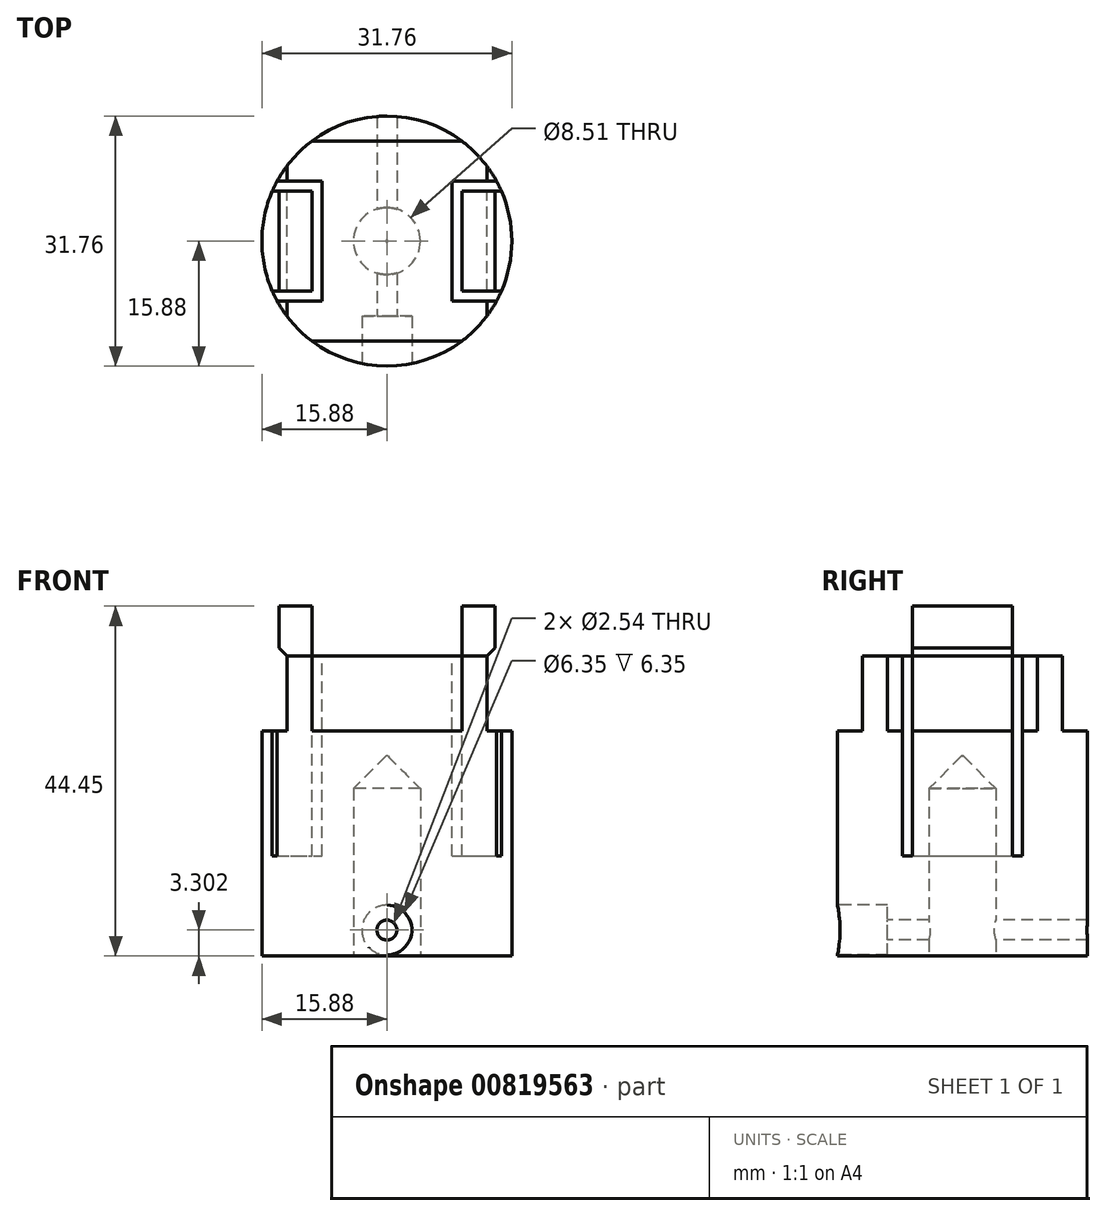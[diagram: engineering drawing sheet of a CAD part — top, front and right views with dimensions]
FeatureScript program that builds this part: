
annotation { "Feature Type Name" : "Feature", "Feature Type Description" : "" }
export const myFeature = defineFeature(function(context is Context, id is Id, definition is map)
    precondition{}
    {
        {
            var Q0;
            Q0=qCreatedBy(makeId("Top.planeOp"),FACE);
            var sketch = newSketch(context, id + "F0", { "sketchPlane" : qUnion([Q0])});
            skCircle(sketch, "E0", {"center": v(0, 0) * mm, "radius": 4.25 * mm});
            skLineSegment(sketch, "E1.bottom", {"start": v(15.88, 15.88) * mm, "end": v(-15.87, 15.88) * mm});
            skLineSegment(sketch, "E1.top", {"start": v(15.87, -15.88) * mm, "end": v(-15.88, -15.88) * mm});
            skLineSegment(sketch, "E1.left", {"start": v(15.88, 15.88) * mm, "end": v(15.88, -15.88) * mm});
            skLineSegment(sketch, "E1.right", {"start": v(-15.88, 15.88) * mm, "end": v(-15.88, -15.88) * mm});
            skSolve(sketch);
        }
        {
            var Q0;
            Q0=makeQuery(id+"F0.imprint","IMPRINT",FACE,{"disambiguationData":[TD([[makeQuery(id+"F0.imprint","IMPRINT",EDGE,{"derivedFrom":sQuery(id+"F0.wireOp",EDGE,"E0")}),-1.0]])]});
            extrude(context, id + "F1", {"entities" : qUnion([Q0]), "depth" : 38.1 * mm, "offsetDistance" : 25.4 * mm});
        }
        {
            var Q0;
            Q0=makeQuery(id+"F1.opExtrude","SWEPT_FACE",FACE,{"disambiguationData":[OSD([sQuery(id+"F0.wireOp",EDGE,"E1.top")])]});
            var sketch = newSketch(context, id + "F2", { "sketchPlane" : qUnion([Q0])});
            skCircle(sketch, "E2", {"center": v(0, 3.3) * mm, "radius": 1.27 * mm});
            skCircle(sketch, "E3", {"center": v(0, 3.3) * mm, "radius": 3.18 * mm});
            skSolve(sketch);
        }
        {
            var Q0;
            Q0=makeQuery(id+"F2.imprint","IMPRINT",FACE,{"disambiguationData":[TD([[makeQuery(id+"F2.imprint","IMPRINT",EDGE,{"derivedFrom":sQuery(id+"F2.wireOp",EDGE,"E2")}),1.0]])]});
            extrude(context, id + "F3", {"entities" : qUnion([Q0]), "operationType" : NewBodyOperationType.REMOVE, "oppositeDirection" : true, "depth" : 76.2 * mm, "offsetDistance" : 25.4 * mm});
        }
        {
            var Q0;
            Q0=makeQuery(id+"F2.imprint","IMPRINT",FACE,{"disambiguationData":[TD([[makeQuery(id+"F2.imprint","IMPRINT",EDGE,{"derivedFrom":sQuery(id+"F2.wireOp",EDGE,"E2")}),-1.0]])]});
            extrude(context, id + "F4", {"entities" : qUnion([Q0]), "operationType" : NewBodyOperationType.REMOVE, "oppositeDirection" : true, "depth" : 6.35 * mm, "offsetDistance" : 25.4 * mm});
        }
        {
            var Q0;
            Q0=makeQuery(id+"F1.opExtrude","CAP_FACE",FACE,{"disambiguationData":[OSD([sQuery(id+"F0.wireOp",EDGE,"E0"),sQuery(id+"F0.wireOp",EDGE,"E1.bottom"),sQuery(id+"F0.wireOp",EDGE,"E1.top"),sQuery(id+"F0.wireOp",EDGE,"E1.left"),sQuery(id+"F0.wireOp",EDGE,"E1.right")])],"isStart":true});
            var sketch = newSketch(context, id + "F5", { "sketchPlane" : qUnion([Q0])});
            skCircle(sketch, "E4", {"center": v(0, 0) * mm, "radius": 15.88 * mm});
            skLineSegment(sketch, "E5.bottom", {"start": v(-15.88, 15.88) * mm, "end": v(15.88, 15.88) * mm});
            skLineSegment(sketch, "E5.top", {"start": v(-15.88, -15.88) * mm, "end": v(15.88, -15.88) * mm});
            skLineSegment(sketch, "E5.left", {"start": v(-15.88, 15.88) * mm, "end": v(-15.88, -15.88) * mm});
            skLineSegment(sketch, "E5.right", {"start": v(15.88, 15.88) * mm, "end": v(15.88, -15.88) * mm});
            skSolve(sketch);
        }
        {
            var Q0;
            Q0=makeQuery(id+"F1.opExtrude","CAP_FACE",FACE,{"disambiguationData":[OSD([sQuery(id+"F0.wireOp",EDGE,"E0"),sQuery(id+"F0.wireOp",EDGE,"E1.bottom"),sQuery(id+"F0.wireOp",EDGE,"E1.top"),sQuery(id+"F0.wireOp",EDGE,"E1.left"),sQuery(id+"F0.wireOp",EDGE,"E1.right")])],"isStart":false});
            var sketch = newSketch(context, id + "F6", { "sketchPlane" : qUnion([Q0])});
            skLineSegment(sketch, "E6.bottom", {"start": v(12.7, -12.7) * mm, "end": v(-12.7, -12.7) * mm});
            skLineSegment(sketch, "E6.top", {"start": v(12.7, 12.7) * mm, "end": v(-12.7, 12.7) * mm});
            skLineSegment(sketch, "E6.left", {"start": v(12.7, -12.7) * mm, "end": v(12.7, 12.7) * mm});
            skLineSegment(sketch, "E6.right", {"start": v(-12.7, -12.7) * mm, "end": v(-12.7, 12.7) * mm});
            skPoint(sketch, "E6.middle", {"position": v(0, 0) * mm});
            skLineSegment(sketch, "E7.bottom", {"start": v(15.88, -15.88) * mm, "end": v(-15.88, -15.88) * mm});
            skLineSegment(sketch, "E7.top", {"start": v(15.88, 15.88) * mm, "end": v(-15.88, 15.87) * mm});
            skLineSegment(sketch, "E7.left", {"start": v(15.88, -15.88) * mm, "end": v(15.88, 15.88) * mm});
            skLineSegment(sketch, "E7.right", {"start": v(-15.88, -15.88) * mm, "end": v(-15.88, 15.88) * mm});
            skSolve(sketch);
        }
        {
            var Q0;
            Q0=makeQuery(id+"F6.imprint","IMPRINT",FACE,{"disambiguationData":[TD([[makeQuery(id+"F6.imprint","IMPRINT",EDGE,{"derivedFrom":sQuery(id+"F6.wireOp",EDGE,"E6.bottom")}),1.0]])]});
            extrude(context, id + "F7", {"entities" : qUnion([Q0]), "operationType" : NewBodyOperationType.REMOVE, "oppositeDirection" : true, "depth" : 9.52 * mm, "offsetDistance" : 25.4 * mm});
        }
        {
            var Q0;
            {var subQ0=sQuery(id+"F5.wireOp",EDGE,"E5.right");var subQ1=sQuery(id+"F5.wireOp",EDGE,"E4");var subQ2=makeQuery(id+"F5.imprint","INTERSECT",VERTEX,{"derivedFrom":[subQ1,subQ0]});Q0=makeQuery(id+"F5.imprint","IMPRINT",FACE,{"disambiguationData":[TD([[makeQuery(id+"F5.imprint","IMPRINT",EDGE,{"disambiguationData":[TD([[subQ2,1.0]])],"derivedFrom":subQ1}),-1.0]])]});}
            var Q1;
            {var subQ0=sQuery(id+"F5.wireOp",EDGE,"E5.left");var subQ1=sQuery(id+"F5.wireOp",EDGE,"E4");var subQ2=makeQuery(id+"F5.imprint","INTERSECT",VERTEX,{"derivedFrom":[subQ1,subQ0]});Q1=makeQuery(id+"F5.imprint","IMPRINT",FACE,{"disambiguationData":[TD([[makeQuery(id+"F5.imprint","IMPRINT",EDGE,{"disambiguationData":[TD([[subQ2,-1.0]])],"derivedFrom":subQ1}),-1.0]])]});}
            var Q2;
            {var subQ0=sQuery(id+"F5.wireOp",EDGE,"E5.bottom");var subQ1=sQuery(id+"F5.wireOp",EDGE,"E4");var subQ2=makeQuery(id+"F5.imprint","INTERSECT",VERTEX,{"derivedFrom":[subQ1,subQ0]});Q2=makeQuery(id+"F5.imprint","IMPRINT",FACE,{"disambiguationData":[TD([[makeQuery(id+"F5.imprint","IMPRINT",EDGE,{"disambiguationData":[TD([[subQ2,-1.0]])],"derivedFrom":subQ1}),-1.0]])]});}
            var Q3;
            {var subQ0=sQuery(id+"F5.wireOp",EDGE,"E5.bottom");var subQ1=sQuery(id+"F5.wireOp",EDGE,"E4");var subQ2=makeQuery(id+"F5.imprint","INTERSECT",VERTEX,{"derivedFrom":[subQ1,subQ0]});Q3=makeQuery(id+"F5.imprint","IMPRINT",FACE,{"disambiguationData":[TD([[makeQuery(id+"F5.imprint","IMPRINT",EDGE,{"disambiguationData":[TD([[subQ2,1.0]])],"derivedFrom":subQ1}),-1.0]])]});}
            extrude(context, id + "F8", {"entities" : qUnion([Q0, Q1, Q2, Q3]), "operationType" : NewBodyOperationType.REMOVE, "oppositeDirection" : true, "depth" : 101.6 * mm, "offsetDistance" : 25.4 * mm});
        }
        {
            var Q0;
            Q0=makeQuery(id+"F1.opExtrude","CAP_FACE",FACE,{"disambiguationData":[OSD([sQuery(id+"F0.wireOp",EDGE,"E0"),sQuery(id+"F0.wireOp",EDGE,"E1.bottom"),sQuery(id+"F0.wireOp",EDGE,"E1.top"),sQuery(id+"F0.wireOp",EDGE,"E1.left"),sQuery(id+"F0.wireOp",EDGE,"E1.right")])],"isStart":false});
            var sketch = newSketch(context, id + "F9", { "sketchPlane" : qUnion([Q0])});
            skLineSegment(sketch, "E8.bottom", {"start": v(-15.88, -7.62) * mm, "end": v(15.88, -7.62) * mm});
            skLineSegment(sketch, "E8.top", {"start": v(-15.88, 7.62) * mm, "end": v(15.88, 7.62) * mm});
            skLineSegment(sketch, "E8.left", {"start": v(-15.88, -7.62) * mm, "end": v(-15.88, 7.62) * mm});
            skLineSegment(sketch, "E8.right", {"start": v(15.88, -7.62) * mm, "end": v(15.88, 7.62) * mm});
            skPoint(sketch, "E8.middle", {"position": v(0, 0) * mm});
            skLineSegment(sketch, "E9.0", {"start": v(8.26, -7.62) * mm, "end": v(8.25, 7.62) * mm});
            skLineSegment(sketch, "E10.0", {"start": v(-8.25, -7.62) * mm, "end": v(-8.26, 7.62) * mm});
            skLineSegment(sketch, "E11.0", {"start": v(-15.88, 6.35) * mm, "end": v(15.88, 6.35) * mm});
            skLineSegment(sketch, "E12.0", {"start": v(-15.88, -6.35) * mm, "end": v(15.88, -6.35) * mm});
            skLineSegment(sketch, "E13.0", {"start": v(-9.52, -7.62) * mm, "end": v(-9.53, 7.62) * mm});
            skLineSegment(sketch, "E14.0", {"start": v(9.53, -7.62) * mm, "end": v(9.52, 7.62) * mm});
            skSolve(sketch);
        }
        {
            var Q0;
            {var subQ0=sQuery(id+"F9.wireOp",EDGE,"E8.left");var subQ1=sQuery(id+"F9.wireOp",EDGE,"E8.top");var subQ2=makeQuery(id+"F9.imprint","INTERSECT",VERTEX,{"derivedFrom":[subQ1,subQ0]});Q0=makeQuery(id+"F9.imprint","IMPRINT",FACE,{"disambiguationData":[TD([[makeQuery(id+"F9.imprint","IMPRINT",EDGE,{"disambiguationData":[TD([[subQ2,-1.0]])],"derivedFrom":subQ1}),-1.0]])]});}
            var Q1;
            {var subQ0=sQuery(id+"F9.wireOp",EDGE,"E13.0");var subQ1=sQuery(id+"F9.wireOp",EDGE,"E8.top");var subQ2=makeQuery(id+"F9.imprint","INTERSECT",VERTEX,{"derivedFrom":[subQ1,subQ0]});Q1=makeQuery(id+"F9.imprint","IMPRINT",FACE,{"disambiguationData":[TD([[makeQuery(id+"F9.imprint","IMPRINT",EDGE,{"disambiguationData":[TD([[subQ2,1.0]])],"derivedFrom":subQ1}),-1.0]])]});}
            var Q2;
            {var subQ0=sQuery(id+"F9.wireOp",EDGE,"E10.0");var subQ1=sQuery(id+"F9.wireOp",EDGE,"E8.top");var subQ2=makeQuery(id+"F9.imprint","INTERSECT",VERTEX,{"derivedFrom":[subQ1,subQ0]});Q2=makeQuery(id+"F9.imprint","IMPRINT",FACE,{"disambiguationData":[TD([[makeQuery(id+"F9.imprint","IMPRINT",EDGE,{"disambiguationData":[TD([[subQ2,1.0]])],"derivedFrom":subQ1}),-1.0]])]});}
            var Q3;
            {var subQ0=sQuery(id+"F9.wireOp",EDGE,"E12.0");var subQ1=sQuery(id+"F9.wireOp",EDGE,"E10.0");var subQ2=makeQuery(id+"F9.imprint","INTERSECT",VERTEX,{"derivedFrom":[subQ1,subQ0]});Q3=makeQuery(id+"F9.imprint","IMPRINT",FACE,{"disambiguationData":[TD([[makeQuery(id+"F9.imprint","IMPRINT",EDGE,{"disambiguationData":[TD([[subQ2,-1.0]])],"derivedFrom":subQ1}),1.0]])]});}
            var Q4;
            {var subQ0=sQuery(id+"F9.wireOp",EDGE,"E10.0");var subQ1=sQuery(id+"F9.wireOp",EDGE,"E8.bottom");var subQ2=makeQuery(id+"F9.imprint","INTERSECT",VERTEX,{"derivedFrom":[subQ1,subQ0]});Q4=makeQuery(id+"F9.imprint","IMPRINT",FACE,{"disambiguationData":[TD([[makeQuery(id+"F9.imprint","IMPRINT",EDGE,{"disambiguationData":[TD([[subQ2,1.0]])],"derivedFrom":subQ1}),1.0]])]});}
            var Q5;
            {var subQ0=sQuery(id+"F9.wireOp",EDGE,"E13.0");var subQ1=sQuery(id+"F9.wireOp",EDGE,"E8.bottom");var subQ2=makeQuery(id+"F9.imprint","INTERSECT",VERTEX,{"derivedFrom":[subQ1,subQ0]});Q5=makeQuery(id+"F9.imprint","IMPRINT",FACE,{"disambiguationData":[TD([[makeQuery(id+"F9.imprint","IMPRINT",EDGE,{"disambiguationData":[TD([[subQ2,1.0]])],"derivedFrom":subQ1}),1.0]])]});}
            var Q6;
            {var subQ0=sQuery(id+"F9.wireOp",EDGE,"E8.left");var subQ1=sQuery(id+"F9.wireOp",EDGE,"E8.bottom");var subQ2=makeQuery(id+"F9.imprint","INTERSECT",VERTEX,{"derivedFrom":[subQ1,subQ0]});Q6=makeQuery(id+"F9.imprint","IMPRINT",FACE,{"disambiguationData":[TD([[makeQuery(id+"F9.imprint","IMPRINT",EDGE,{"disambiguationData":[TD([[subQ2,-1.0]])],"derivedFrom":subQ1}),1.0]])]});}
            var Q7;
            {var subQ0=sQuery(id+"F9.wireOp",EDGE,"E8.right");var subQ1=sQuery(id+"F9.wireOp",EDGE,"E8.top");var subQ2=makeQuery(id+"F9.imprint","INTERSECT",VERTEX,{"derivedFrom":[subQ1,subQ0]});Q7=makeQuery(id+"F9.imprint","IMPRINT",FACE,{"disambiguationData":[TD([[makeQuery(id+"F9.imprint","IMPRINT",EDGE,{"disambiguationData":[TD([[subQ2,1.0]])],"derivedFrom":subQ1}),-1.0]])]});}
            var Q8;
            {var subQ0=sQuery(id+"F9.wireOp",EDGE,"E14.0");var subQ1=sQuery(id+"F9.wireOp",EDGE,"E8.top");var subQ2=makeQuery(id+"F9.imprint","INTERSECT",VERTEX,{"derivedFrom":[subQ1,subQ0]});Q8=makeQuery(id+"F9.imprint","IMPRINT",FACE,{"disambiguationData":[TD([[makeQuery(id+"F9.imprint","IMPRINT",EDGE,{"disambiguationData":[TD([[subQ2,-1.0]])],"derivedFrom":subQ1}),-1.0]])]});}
            var Q9;
            {var subQ0=sQuery(id+"F9.wireOp",EDGE,"E9.0");var subQ1=sQuery(id+"F9.wireOp",EDGE,"E8.top");var subQ2=makeQuery(id+"F9.imprint","INTERSECT",VERTEX,{"derivedFrom":[subQ1,subQ0]});Q9=makeQuery(id+"F9.imprint","IMPRINT",FACE,{"disambiguationData":[TD([[makeQuery(id+"F9.imprint","IMPRINT",EDGE,{"disambiguationData":[TD([[subQ2,-1.0]])],"derivedFrom":subQ1}),-1.0]])]});}
            var Q10;
            {var subQ0=sQuery(id+"F9.wireOp",EDGE,"E12.0");var subQ1=sQuery(id+"F9.wireOp",EDGE,"E9.0");var subQ2=makeQuery(id+"F9.imprint","INTERSECT",VERTEX,{"derivedFrom":[subQ1,subQ0]});Q10=makeQuery(id+"F9.imprint","IMPRINT",FACE,{"disambiguationData":[TD([[makeQuery(id+"F9.imprint","IMPRINT",EDGE,{"disambiguationData":[TD([[subQ2,-1.0]])],"derivedFrom":subQ1}),-1.0]])]});}
            var Q11;
            {var subQ0=sQuery(id+"F9.wireOp",EDGE,"E9.0");var subQ1=sQuery(id+"F9.wireOp",EDGE,"E8.bottom");var subQ2=makeQuery(id+"F9.imprint","INTERSECT",VERTEX,{"derivedFrom":[subQ1,subQ0]});Q11=makeQuery(id+"F9.imprint","IMPRINT",FACE,{"disambiguationData":[TD([[makeQuery(id+"F9.imprint","IMPRINT",EDGE,{"disambiguationData":[TD([[subQ2,-1.0]])],"derivedFrom":subQ1}),1.0]])]});}
            var Q12;
            {var subQ0=sQuery(id+"F9.wireOp",EDGE,"E14.0");var subQ1=sQuery(id+"F9.wireOp",EDGE,"E8.bottom");var subQ2=makeQuery(id+"F9.imprint","INTERSECT",VERTEX,{"derivedFrom":[subQ1,subQ0]});Q12=makeQuery(id+"F9.imprint","IMPRINT",FACE,{"disambiguationData":[TD([[makeQuery(id+"F9.imprint","IMPRINT",EDGE,{"disambiguationData":[TD([[subQ2,-1.0]])],"derivedFrom":subQ1}),1.0]])]});}
            var Q13;
            {var subQ0=sQuery(id+"F9.wireOp",EDGE,"E8.right");var subQ1=sQuery(id+"F9.wireOp",EDGE,"E8.bottom");var subQ2=makeQuery(id+"F9.imprint","INTERSECT",VERTEX,{"derivedFrom":[subQ1,subQ0]});Q13=makeQuery(id+"F9.imprint","IMPRINT",FACE,{"disambiguationData":[TD([[makeQuery(id+"F9.imprint","IMPRINT",EDGE,{"disambiguationData":[TD([[subQ2,1.0]])],"derivedFrom":subQ1}),1.0]])]});}
            extrude(context, id + "F10", {"entities" : qUnion([Q0, Q1, Q2, Q3, Q4, Q5, Q6, Q7, Q8, Q9, Q10, Q11, Q12, Q13]), "operationType" : NewBodyOperationType.REMOVE, "oppositeDirection" : true, "depth" : 25.4 * mm, "offsetDistance" : 25.4 * mm});
        }
        {
            var Q0;
            {var subQ5=sQuery(id+"F9.wireOp",EDGE,"E14.0");Q0=makeQuery(id+"F10.boolean.opBoolean","SPLIT",FACE,{"disambiguationData":[TD([makeQuery(id+"F10.opExtrude","SWEPT_FACE",FACE,{"disambiguationData":[OSD([subQ5])]})])],"derivedFrom":makeQuery(id+"F1.opExtrude","CAP_FACE",FACE,{"disambiguationData":[OSD([sQuery(id+"F0.wireOp",EDGE,"E0"),sQuery(id+"F0.wireOp",EDGE,"E1.bottom"),sQuery(id+"F0.wireOp",EDGE,"E1.top"),sQuery(id+"F0.wireOp",EDGE,"E1.left"),sQuery(id+"F0.wireOp",EDGE,"E1.right")])],"isStart":false})});}
            var sketch = newSketch(context, id + "F11", { "sketchPlane" : qUnion([Q0])});
            skLineSegment(sketch, "E15.bottom", {"start": v(9.53, -6.35) * mm, "end": v(13.72, -6.35) * mm});
            skLineSegment(sketch, "E15.top", {"start": v(9.53, 6.35) * mm, "end": v(13.72, 6.35) * mm});
            skLineSegment(sketch, "E15.left", {"start": v(9.53, -6.35) * mm, "end": v(9.53, 6.35) * mm});
            skLineSegment(sketch, "E15.right", {"start": v(13.72, -6.35) * mm, "end": v(13.72, 6.35) * mm});
            skLineSegment(sketch, "E16.MirrorCS", {"start": v(-9.53, -6.35) * mm, "end": v(-13.72, -6.35) * mm});
            skLineSegment(sketch, "E17.MirrorCS", {"start": v(-9.53, 6.35) * mm, "end": v(-13.72, 6.35) * mm});
            skLineSegment(sketch, "E18.MirrorCS", {"start": v(-13.72, -6.35) * mm, "end": v(-13.72, 6.35) * mm});
            skLineSegment(sketch, "E19.MirrorCS", {"start": v(-9.53, -6.35) * mm, "end": v(-9.53, 6.35) * mm});
            skSolve(sketch);
        }
        {
            var Q0;
            {var subQ0=sQuery(id+"F11.wireOp",EDGE,"E15.left");Q0=makeQuery(id+"F11.imprint","IMPRINT",FACE,{"disambiguationData":[TD([[makeQuery(id+"F11.imprint","IMPRINT",EDGE,{"derivedFrom":subQ0}),-1.0]])]});}
            var Q1;
            {var subQ10=sQuery(id+"F11.wireOp",EDGE,"E15.right");Q1=makeQuery(id+"F11.imprint","IMPRINT",FACE,{"disambiguationData":[TD([[makeQuery(id+"F11.imprint","IMPRINT",EDGE,{"derivedFrom":subQ10}),1.0]])]});}
            var Q2;
            Q2=makeQuery(id+"F11.imprint","IMPRINT",FACE,{"disambiguationData":[TD([[makeQuery(id+"F11.imprint","IMPRINT",EDGE,{"derivedFrom":sQuery(id+"F11.wireOp",EDGE,"E16.MirrorCS")}),-1.0]])]});
            extrude(context, id + "F12", {"entities" : qUnion([Q0, Q1, Q2]), "operationType" : NewBodyOperationType.ADD, "depth" : 6.35 * mm, "offsetDistance" : 25.4 * mm});
        }
        {
            var Q0;
            Q0=makeQuery(id+"F12.opExtrude","CAP_EDGE",EDGE,{"disambiguationData":[OSD([sQuery(id+"F11.wireOp",EDGE,"E15.right")])],"isStart":true});
            var Q1;
            Q1=makeQuery(id+"F12.opExtrude","CAP_EDGE",EDGE,{"disambiguationData":[OSD([sQuery(id+"F11.wireOp",EDGE,"E18.MirrorCS")])],"isStart":true});
            chamfer(context, id + "F13", {"entities" : qUnion([Q0, Q1]), "width" : 1.02 * mm, "tangentPropagation" : true});
        }
        {
            var Q0;
            {var subQ25=sQuery(id+"F0.wireOp",EDGE,"E0");Q0=makeQuery(id+"F10.boolean.opBoolean","SPLIT",FACE,{"disambiguationData":[TD([makeQuery(id+"F1.opExtrude","SWEPT_FACE",FACE,{"disambiguationData":[OSD([subQ25])]})])],"derivedFrom":makeQuery(id+"F1.opExtrude","CAP_FACE",FACE,{"disambiguationData":[OSD([subQ25,sQuery(id+"F0.wireOp",EDGE,"E1.bottom"),sQuery(id+"F0.wireOp",EDGE,"E1.top"),sQuery(id+"F0.wireOp",EDGE,"E1.left"),sQuery(id+"F0.wireOp",EDGE,"E1.right")])],"isStart":false})});}
            var sketch = newSketch(context, id + "F14", { "sketchPlane" : qUnion([Q0])});
            skLineSegment(sketch, "E20.bottom", {"start": v(6.35, 6.35) * mm, "end": v(-6.35, 6.35) * mm});
            skLineSegment(sketch, "E20.top", {"start": v(6.35, -6.35) * mm, "end": v(-6.35, -6.35) * mm});
            skLineSegment(sketch, "E20.left", {"start": v(6.35, 6.35) * mm, "end": v(6.35, -6.35) * mm});
            skLineSegment(sketch, "E20.right", {"start": v(-6.35, 6.35) * mm, "end": v(-6.35, -6.35) * mm});
            skPoint(sketch, "E20.middle", {"position": v(0, 0) * mm});
            skSolve(sketch);
        }
        {
            var Q0;
            Q0=makeQuery(id+"F14.imprint","IMPRINT",FACE,{"disambiguationData":[TD([[makeQuery(id+"F14.imprint","IMPRINT",EDGE,{"derivedFrom":sQuery(id+"F14.wireOp",EDGE,"E20.bottom")}),1.0]])]});
            var Q1;
            Q1=makeQuery(id+"F14.imprint","IMPRINT",FACE,{"disambiguationData":[TD([[makeQuery(id+"F14.imprint","IMPRINT",EDGE,{"derivedFrom":makeQuery(id+"F1.opExtrude","CAP_EDGE",EDGE,{"disambiguationData":[OSD([sQuery(id+"F0.wireOp",EDGE,"E0")])],"isStart":false})}),1.0]])]});
            extrude(context, id + "F15", {"entities" : qUnion([Q0, Q1]), "operationType" : NewBodyOperationType.ADD, "oppositeDirection" : true, "depth" : 12.7 * mm, "offsetDistance" : 25.4 * mm});
        }
        {
            var Q0;
            Q0=makeQuery(id+"F15.boolean.opBoolean","INTERSECT",EDGE,{"derivedFrom":[makeQuery(id+"F1.opExtrude","SWEPT_FACE",FACE,{"disambiguationData":[OSD([sQuery(id+"F0.wireOp",EDGE,"E0")])]}),makeQuery(id+"F15.opExtrude","CAP_FACE",FACE,{"disambiguationData":[OSD([sQuery(id+"F14.wireOp",EDGE,"E20.bottom"),sQuery(id+"F14.wireOp",EDGE,"E20.top"),sQuery(id+"F14.wireOp",EDGE,"E20.left"),sQuery(id+"F14.wireOp",EDGE,"E20.right")])],"isStart":false})]});
            chamfer(context, id + "F16", {"entities" : qUnion([Q0]), "width" : 4.13 * mm, "tangentPropagation" : true});
        }
    });
